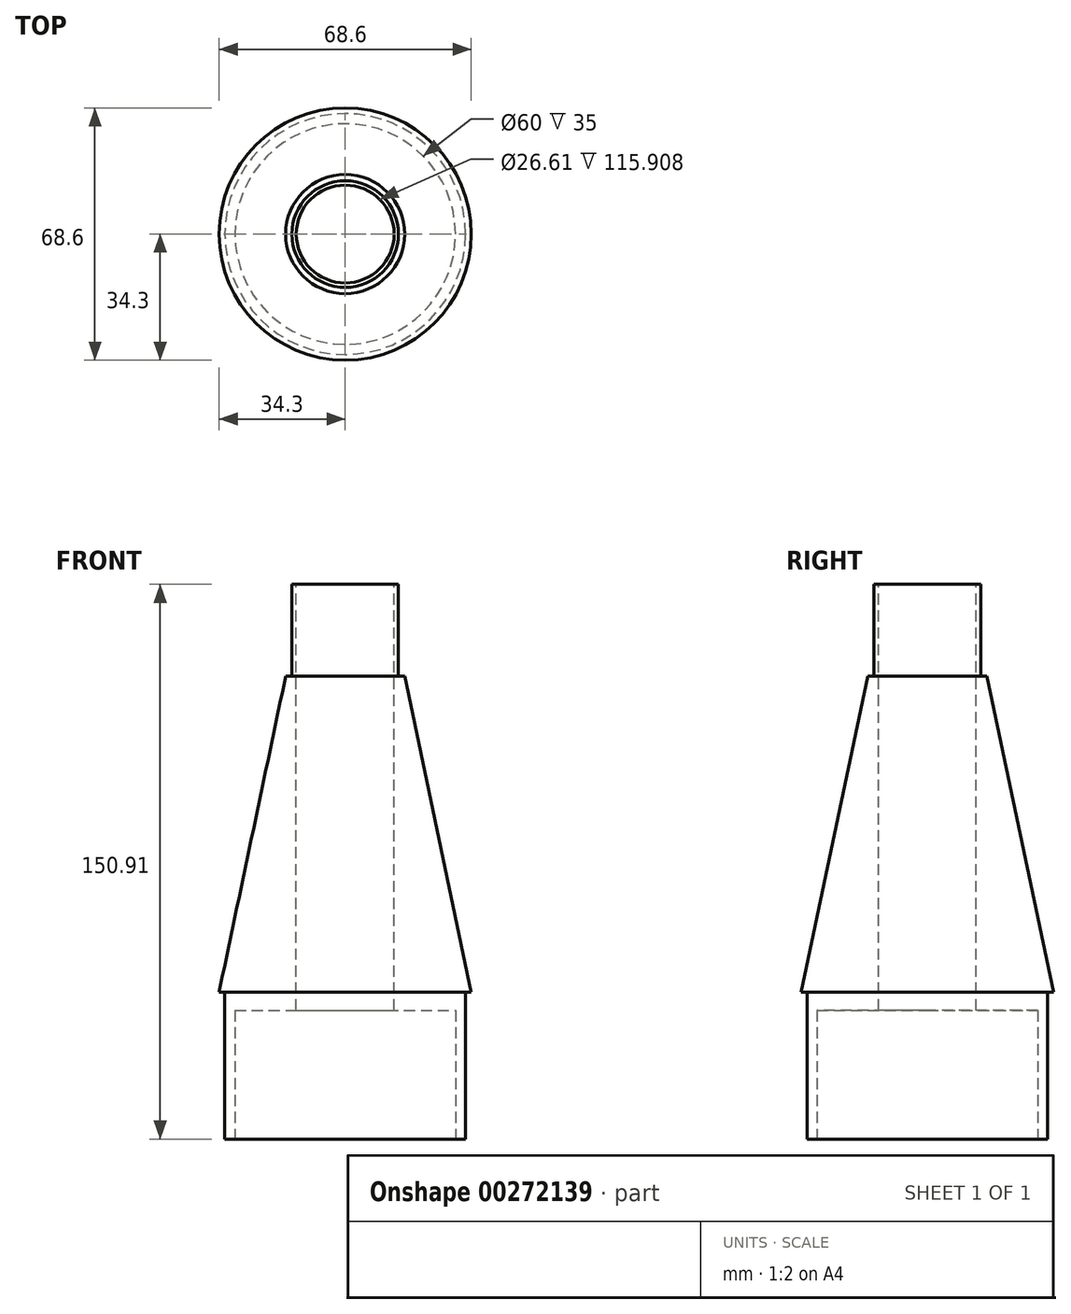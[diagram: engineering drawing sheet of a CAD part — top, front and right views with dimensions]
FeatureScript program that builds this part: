
annotation { "Feature Type Name" : "Feature", "Feature Type Description" : "" }
export const myFeature = defineFeature(function(context is Context, id is Id, definition is map)
    precondition{}
    {
        {
            var Q0;
            Q0=qCreatedBy(makeId("Front.planeOp"),FACE);
            var sketch = newSketch(context, id + "F0", { "sketchPlane" : qUnion([Q0])});
            skLineSegment(sketch, "E0", {"start": v(0, 140.92) * mm, "end": v(0, 55) * mm});
            skLineSegment(sketch, "E1", {"start": v(0, 55) * mm, "end": v(34.3, 55) * mm});
            skLineSegment(sketch, "E2", {"start": v(0, 140.92) * mm, "end": v(16.2, 140.92) * mm});
            skLineSegment(sketch, "E3", {"start": v(0, -30.9) * mm, "end": v(0, 140.92) * mm});
            skLineSegment(sketch, "E4", {"start": v(16.2, 140.92) * mm, "end": v(34.3, 55) * mm});
            skSolve(sketch);
        }
        {
            var Q0;
            {var subQ0=sQuery(id+"F0.wireOp",EDGE,"E1");Q0=makeQuery(id+"F0.imprint","IMPRINT",FACE,{"disambiguationData":[TD([[makeQuery(id+"F0.imprint","IMPRINT",EDGE,{"derivedFrom":subQ0}),1.0]])]});}
            var Q1;
            Q1=sQuery(id+"F0.wireOp",EDGE,"E3");
            revolve(context, id + "F1", {"entities" : qUnion([Q0]), "axis" : qUnion([Q1]), "revolveType" : RevolveType.FULL});
        }
        {
            var Q0;
            Q0=makeQuery(id+"F1.opRevolve","SWEPT_FACE",FACE,{"disambiguationData":[OSD([sQuery(id+"F0.wireOp",EDGE,"E1")])]});
            var sketch = newSketch(context, id + "F2", { "sketchPlane" : qUnion([Q0])});
            skCircle(sketch, "E5", {"center": v(0, 0) * mm, "radius": 32.75 * mm});
            skSolve(sketch);
        }
        {
            var Q0;
            Q0=makeQuery(id+"F2.imprint","IMPRINT",FACE,{"disambiguationData":[TD([[makeQuery(id+"F2.imprint","IMPRINT",EDGE,{"derivedFrom":sQuery(id+"F2.wireOp",EDGE,"E5")}),1.0]])]});
            extrude(context, id + "F3", {"entities" : qUnion([Q0]), "operationType" : NewBodyOperationType.ADD, "depth" : 40 * mm});
        }
        {
            var Q0;
            Q0=makeQuery(id+"F3.opExtrude","CAP_FACE",FACE,{"disambiguationData":[OSD([sQuery(id+"F2.wireOp",EDGE,"E5")])],"isStart":false});
            var sketch = newSketch(context, id + "F4", { "sketchPlane" : qUnion([Q0])});
            skCircle(sketch, "E6", {"center": v(0, 0) * mm, "radius": 30 * mm});
            skSolve(sketch);
        }
        {
            var Q0;
            Q0=makeQuery(id+"F4.imprint","IMPRINT",FACE,{"disambiguationData":[TD([[makeQuery(id+"F4.imprint","IMPRINT",EDGE,{"derivedFrom":sQuery(id+"F4.wireOp",EDGE,"E6")}),1.0]])]});
            extrude(context, id + "F5", {"entities" : qUnion([Q0]), "operationType" : NewBodyOperationType.REMOVE, "oppositeDirection" : true, "depth" : 35 * mm});
        }
        {
            var Q0;
            Q0=makeQuery(id+"F1.opRevolve","SWEPT_FACE",FACE,{"disambiguationData":[OSD([sQuery(id+"F0.wireOp",EDGE,"E2")])]});
            var sketch = newSketch(context, id + "F6", { "sketchPlane" : qUnion([Q0])});
            skSolve(sketch);
        }
        {
            var Q0;
            Q0=makeQuery(id+"F6.imprint","IMPRINT",FACE,{"disambiguationData":[TD([[makeQuery(id+"F6.imprint","IMPRINT",EDGE,{"derivedFrom":makeQuery(id+"F1.opRevolve","SWEPT_EDGE",EDGE,{"disambiguationData":[OSD([sQuery(id+"F0.wireOp",EDGE,"E2"),sQuery(id+"F0.wireOp",EDGE,"ihLGtoGn-mvP1-avwc-MOmJ-ta9pTefaUMV7")])]})}),-1.0]])]});
            var sketch = newSketch(context, id + "F7", { "sketchPlane" : qUnion([Q0])});
            skCircle(sketch, "E7", {"center": v(0, 0) * mm, "radius": 14.5 * mm});
            skSolve(sketch);
        }
        {
            var Q0;
            Q0=makeQuery(id+"F7.imprint","IMPRINT",FACE,{"disambiguationData":[TD([[makeQuery(id+"F7.imprint","IMPRINT",EDGE,{"derivedFrom":sQuery(id+"F7.wireOp",EDGE,"E7")}),1.0]])]});
            extrude(context, id + "F8", {"entities" : qUnion([Q0]), "operationType" : NewBodyOperationType.ADD, "depth" : 25 * mm});
        }
        {
            var Q0;
            Q0=makeQuery(id+"F8.opExtrude","CAP_FACE",FACE,{"disambiguationData":[OSD([sQuery(id+"F7.wireOp",EDGE,"E7")])],"isStart":false});
            var sketch = newSketch(context, id + "F9", { "sketchPlane" : qUnion([Q0])});
            skCircle(sketch, "E8", {"center": v(0, 0) * mm, "radius": 13.3 * mm});
            skSolve(sketch);
        }
        {
            var Q0;
            Q0=makeQuery(id+"F9.imprint","IMPRINT",FACE,{"disambiguationData":[TD([[makeQuery(id+"F9.imprint","IMPRINT",EDGE,{"derivedFrom":sQuery(id+"F9.wireOp",EDGE,"E8")}),1.0]])]});
            extrude(context, id + "F10", {"entities" : qUnion([Q0]), "operationType" : NewBodyOperationType.REMOVE, "oppositeDirection" : true, "depth" : 140 * mm});
        }
    });
